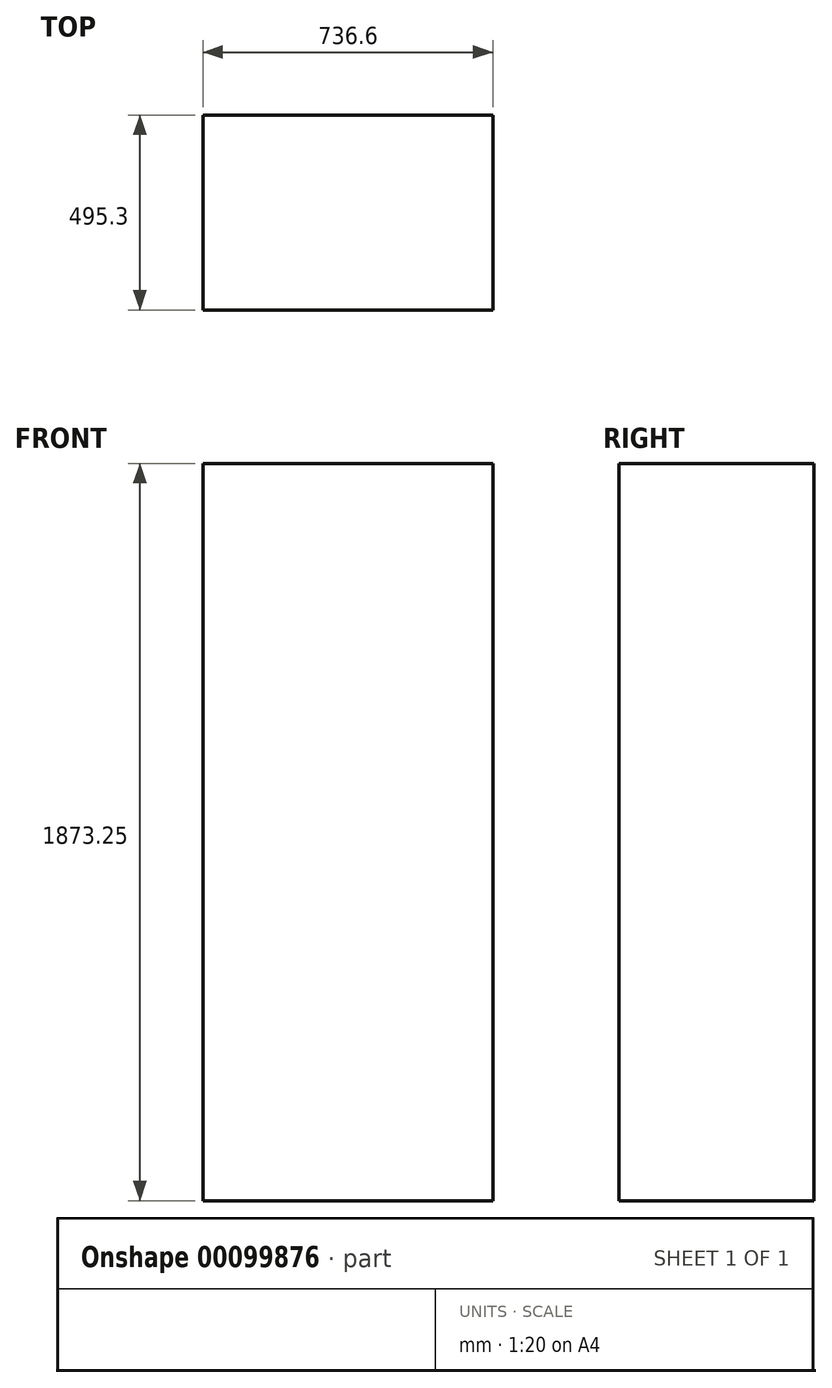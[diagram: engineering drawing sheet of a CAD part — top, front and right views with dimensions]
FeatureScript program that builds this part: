
annotation { "Feature Type Name" : "Feature", "Feature Type Description" : "" }
export const myFeature = defineFeature(function(context is Context, id is Id, definition is map)
    precondition{}
    {
        {
            var Q0;
            Q0=qCreatedBy(makeId("Top.planeOp"),FACE);
            var sketch = newSketch(context, id + "F0", { "sketchPlane" : qUnion([Q0])});
            skLineSegment(sketch, "E0.bottom", {"start": v(368.3, 247.65) * mm, "end": v(-368.3, 247.65) * mm});
            skLineSegment(sketch, "E0.top", {"start": v(368.3, -247.65) * mm, "end": v(-368.3, -247.65) * mm});
            skLineSegment(sketch, "E0.left", {"start": v(368.3, 247.65) * mm, "end": v(368.3, -247.65) * mm});
            skLineSegment(sketch, "E0.right", {"start": v(-368.3, 247.65) * mm, "end": v(-368.3, -247.65) * mm});
            skPoint(sketch, "E0.middle", {"position": v(0, 0) * mm});
            skSolve(sketch);
        }
        {
            var Q0;
            Q0=qSketchRegion(id+"F0",true);
            extrude(context, id + "F1", {"entities" : qUnion([Q0]), "depth" : 1873.25 * mm});
        }
    });
